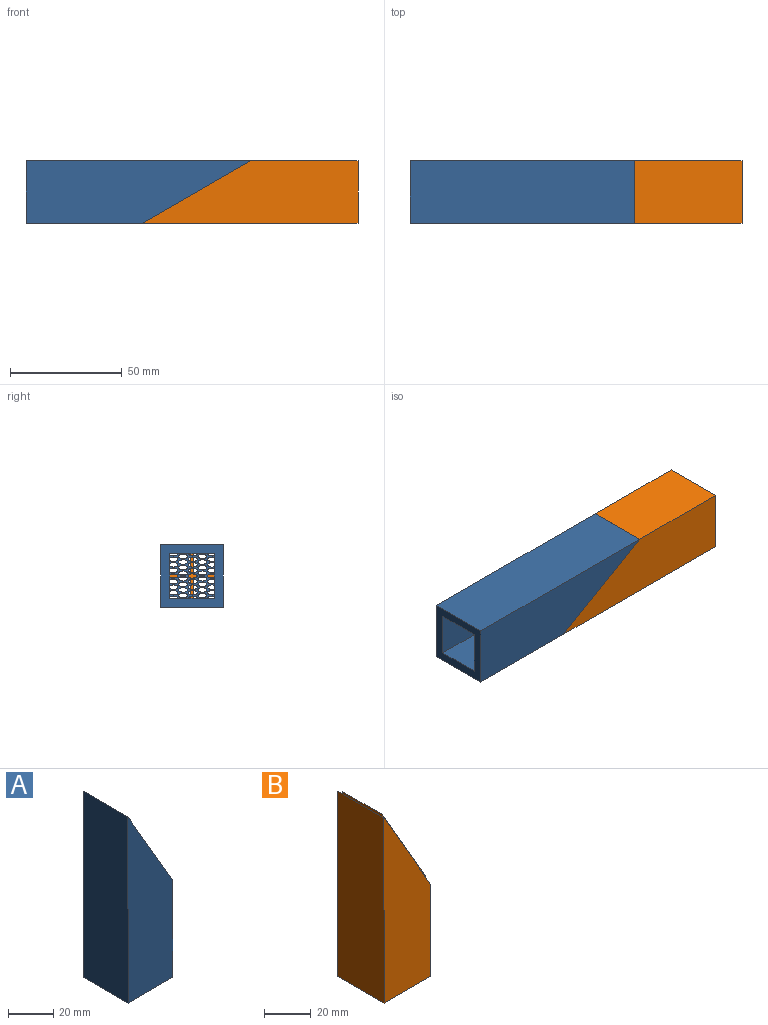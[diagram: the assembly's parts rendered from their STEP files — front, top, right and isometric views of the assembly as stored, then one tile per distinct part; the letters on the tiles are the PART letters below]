
ASSEMBLY  parts=2 mates=1
PART A: 59 faces, bbox 28x28x100.5 mm
  f0: plane 56.93x20mm, normal (-1,0,0), area 1119.9mm2, adj f1,f2,f3,f4,f17,f18,f19,f52
  f1: plane 91.57x20mm, normal (0,1,0), area 1472.7mm2, adj f0,f3,f4,f9,f19,f20,f21,f22
  f2: plane 91.57x20mm, normal (0,-1,0), area 1462.3mm2, adj f0,f3,f4,f9,f10,f11,f12,f13
  f3: plane 28x28mm, normal (0,0,-1), area 384mm2, adj f0,f1,f2,f5,f6,f7,f8,f9
  f4: plane 45.21x26.1mm, normal (0.87,0,0.5), area 784mm2, adj f0,f1,f2,f9,f10,f11,f12,f13
  f5: plane 100.5x28mm, normal (0,1,0), area 2135mm2, adj f3,f6,f8,f54
  f6: plane 100.5x28mm, normal (-1,0,0), area 2813.9mm2, adj f3,f5,f7,f54
  f7: plane 100.5x28mm, normal (0,-1,0), area 2135mm2, adj f3,f6,f8,f54
  f8: plane 52x28mm, normal (1,0,0), area 1456mm2, adj f3,f5,f7,f54
  f9: plane 91.57x20mm, normal (1,0,0), area 1812.7mm2, adj f1,f2,f3,f4,f27,f28,f29,f52
  f10: bspline ~7.44x3.68mm, area 16.8mm2, adj f2,f4,f52
  f11: bspline ~7.44x3.68mm, area 16.8mm2, adj f2,f4,f52
  f12: bspline ~7.44x3.68mm, area 16.8mm2, adj f2,f4,f52
  f13: bspline ~7.44x3.68mm, area 16.8mm2, adj f2,f4,f52
  f14: bspline ~7.44x3.68mm, area 16.8mm2, adj f2,f4,f52
  f15: bspline ~7.44x3.68mm, area 16.8mm2, adj f2,f4,f52
  f16: bspline ~7.44x3.68mm, area 16.8mm2, adj f2,f4,f52
  f17: bspline ~4.72x3.68mm, area 8.4mm2, adj f0,f2,f4,f52
  f18: bspline ~5.46x4mm, area 9.7mm2, adj f0,f4,f52
  f19: bspline ~4.25x3mm, area 6.9mm2, adj f0,f1,f4,f52
  f20: bspline ~6.5x3mm, area 13.7mm2, adj f1,f4,f52
  f21: bspline ~6.5x3mm, area 13.7mm2, adj f1,f4,f52
  f22: bspline ~6.5x3mm, area 13.7mm2, adj f1,f4,f52
  f23: bspline ~6.5x3mm, area 13.7mm2, adj f1,f4,f52
  f24: bspline ~6.5x3mm, area 13.7mm2, adj f1,f4,f52
  f25: bspline ~6.5x3mm, area 13.7mm2, adj f1,f4,f52
  f26: bspline ~6.5x3mm, area 13.7mm2, adj f1,f4,f52
  f27: bspline ~4.25x3mm, area 6.9mm2, adj f1,f4,f9,f52
  f28: bspline ~5.46x4mm, area 9.7mm2, adj f4,f9,f52
  f29: bspline ~4.72x3.68mm, area 8.4mm2, adj f2,f4,f9,f52
  f30: bspline ~8.93x4mm, area 19.4mm2, adj f4,f52
  f31: bspline ~8.93x4mm, area 19.4mm2, adj f4,f52
  f32: bspline ~8.93x4mm, area 19.4mm2, adj f4,f52
  f33: bspline ~8.93x4mm, area 19.4mm2, adj f4,f52
  f34: bspline ~8.93x4mm, area 19.4mm2, adj f4,f52
  f35: bspline ~8.93x4mm, area 19.4mm2, adj f4,f52
  f36: bspline ~8.93x4mm, area 19.4mm2, adj f4,f52
  f37: bspline ~8.93x4mm, area 19.4mm2, adj f4,f52
  f38: bspline ~8.93x4mm, area 19.4mm2, adj f4,f52
  f39: bspline ~8.93x4mm, area 19.4mm2, adj f4,f52
  f40: bspline ~8.93x4mm, area 19.4mm2, adj f4,f52
  f41: bspline ~8.93x4mm, area 19.4mm2, adj f4,f52
  f42: bspline ~8.93x4mm, area 19.4mm2, adj f4,f52
  f43: bspline ~8.93x4mm, area 19.4mm2, adj f4,f52
  f44: bspline ~8.93x4mm, area 19.4mm2, adj f4,f52
  f45: bspline ~8.93x4mm, area 19.4mm2, adj f4,f52
  f46: bspline ~8.93x4mm, area 19.4mm2, adj f4,f52
  f47: bspline ~8.93x4mm, area 19.4mm2, adj f4,f52
  f48: bspline ~8.93x4mm, area 19.4mm2, adj f4,f52
  f49: bspline ~8.93x4mm, area 19.4mm2, adj f4,f52
  f50: bspline ~8.93x4mm, area 19.4mm2, adj f4,f52
  f51: bspline ~8.93x4mm, area 19.4mm2, adj f4,f52
  f52: plane 34.64x20mm, normal (-0.87,0,-0.5), area 320.8mm2, adj f0,f1,f2,f9,f10,f11,f12,f13
  f53: bspline ~8.93x4mm, area 19.4mm2, adj f4,f52
  f54: plane 48.5x28mm, normal (0.87,0,0.5), area 304.8mm2, adj f5,f6,f7,f8,f55,f56,f57,f58
  f55: plane 24.2x2mm, normal (-1,0,0), area 48.4mm2, adj f4,f54,f56,f58
  f56: plane 47.21x26.1mm, normal (0,1,0), area 52.2mm2, adj f4,f54,f55,f57
  f57: plane 24.2x2mm, normal (1,0,0), area 48.4mm2, adj f4,f54,f56,f58
  f58: plane 47.21x26.1mm, normal (0,-1,0), area 52.2mm2, adj f4,f54,f55,f57
PART B: 24 faces, bbox 28x28x96.7 mm
  f0: plane 48x28mm, normal (1,0,0), area 1344mm2, adj f4,f5,f7,f19
  f1: plane 44.86x25.9mm, normal (0.87,0,0.5), area 510.8mm2, adj f2,f3,f8,f9,f11,f12,f13,f14
  f2: plane 56.93x20mm, normal (-1,0,0), area 1136.6mm2, adj f1,f3,f4,f9,f10,f15,f16
  f3: plane 91.57x20mm, normal (0,1,0), area 1483mm2, adj f1,f2,f4,f8,f10,f17,f18
  f4: plane 28x28mm, normal (0,0,-1), area 384mm2, adj f0,f2,f3,f5,f6,f7,f8,f9
  f5: plane 96.5x28mm, normal (0,1,0), area 2023mm2, adj f0,f4,f6,f19
  f6: plane 96.5x28mm, normal (-1,0,0), area 2701.9mm2, adj f4,f5,f7,f19
  f7: plane 96.5x28mm, normal (0,-1,0), area 2023mm2, adj f0,f4,f6,f19
  f8: plane 91.57x20mm, normal (1,0,0), area 1829.4mm2, adj f1,f3,f4,f9,f10,f11,f12
  f9: plane 91.57x20mm, normal (0,-1,0), area 1483mm2, adj f1,f2,f4,f8,f10,f13,f14
  f10: plane 34.64x20mm, normal (-0.87,0,-0.5), area 78mm2, adj f2,f3,f8,f9,f11,f12,f13,f14
  f11: plane 18.45x9.5mm, normal (0,-1,0), area 19mm2, adj f1,f8,f10,f18
  f12: plane 18.45x9.5mm, normal (0,1,0), area 19mm2, adj f1,f8,f10,f13
  f13: plane 9.5x2mm, normal (-1,0,0), area 19mm2, adj f1,f9,f10,f12
  f14: plane 9.5x2mm, normal (1,0,0), area 19mm2, adj f1,f9,f10,f15
  f15: plane 18.45x9.5mm, normal (0,1,0), area 19mm2, adj f1,f2,f10,f14
  f16: plane 18.45x9.5mm, normal (0,-1,0), area 19mm2, adj f1,f2,f10,f17
  f17: plane 9.5x2mm, normal (1,0,0), area 19mm2, adj f1,f3,f10,f16
  f18: plane 9.5x2mm, normal (-1,0,0), area 19mm2, adj f1,f3,f10,f11
  f19: plane 48.5x28mm, normal (0.87,0,0.5), area 335.2mm2, adj f0,f5,f6,f7,f20,f21,f22,f23
  f20: plane 23.8x2mm, normal (1,0,0), area 47.6mm2, adj f1,f19,f21,f23
  f21: plane 46.86x25.9mm, normal (0,1,0), area 51.8mm2, adj f1,f19,f20,f22
  f22: plane 23.8x2mm, normal (-1,0,0), area 47.6mm2, adj f1,f19,f21,f23
  f23: plane 46.86x25.9mm, normal (0,-1,0), area 51.8mm2, adj f1,f19,f20,f22
PLACE A rot(axis=(0,1,0),90deg) t=(-171.87,27.07,56.55)mm
PLACE B rot(axis=(0,-1,0),90deg) t=(-23.37,27.07,28.55)mm
MATE fastened B.f1 <-> A.f4  axis (-0.5,0,0.87) through (-97.62,41.07,42.55)mm
